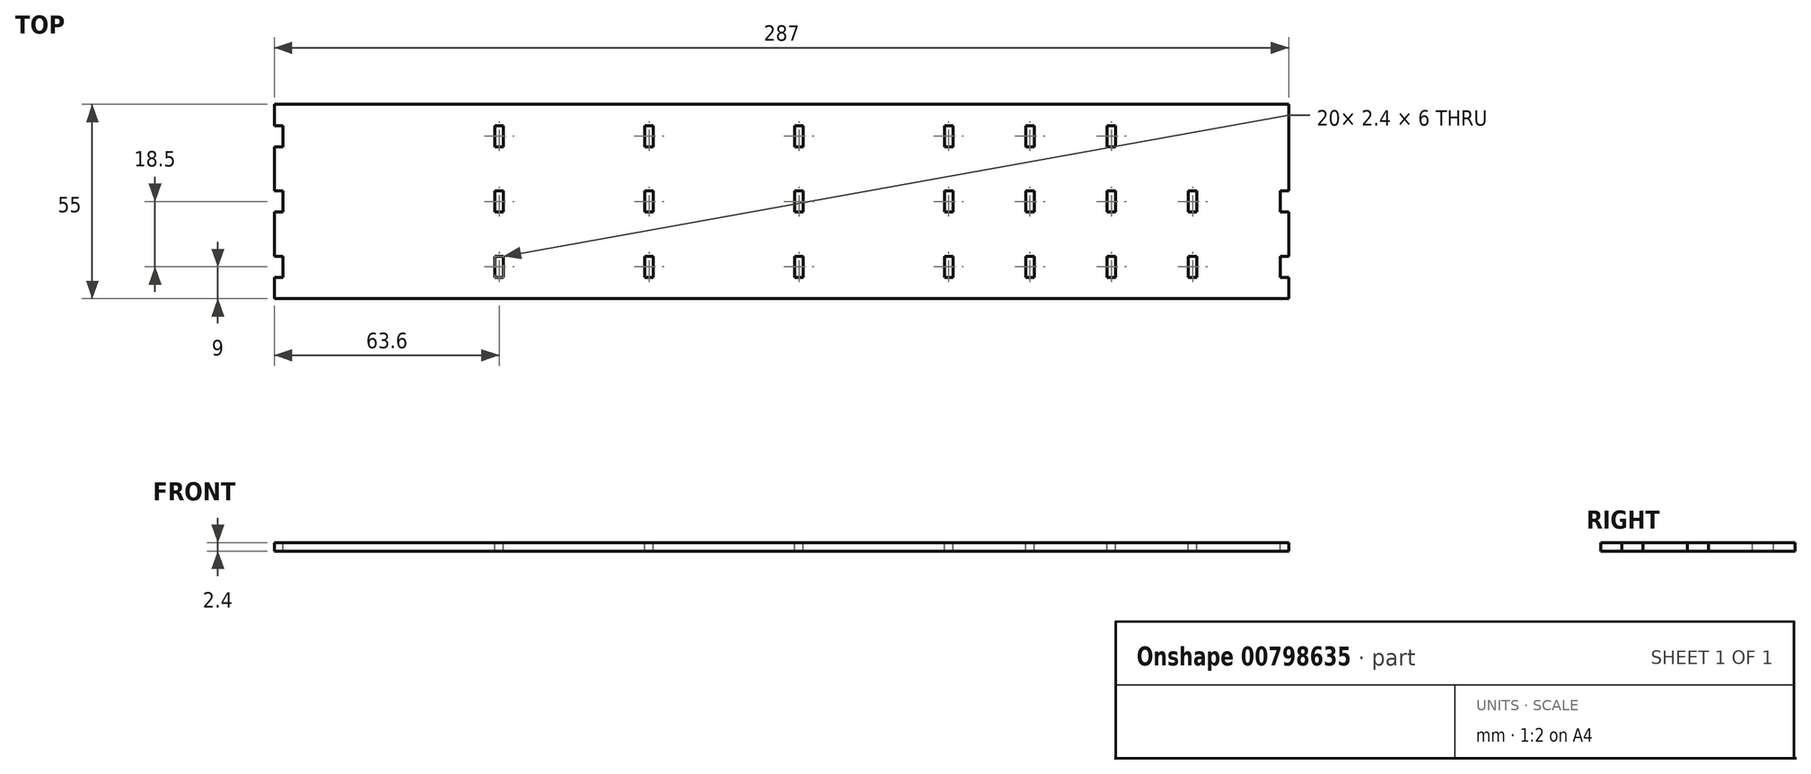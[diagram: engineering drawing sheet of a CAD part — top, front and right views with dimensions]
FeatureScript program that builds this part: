
annotation { "Feature Type Name" : "Feature", "Feature Type Description" : "" }
export const myFeature = defineFeature(function(context is Context, id is Id, definition is map)
    precondition{}
    {
        {
            var Q0;
            Q0=qCreatedBy(makeId("Top.planeOp"),FACE);
            var sketch = newSketch(context, id + "F0", { "sketchPlane" : qUnion([Q0])});
            skLineSegment(sketch, "E0.bottom", {"start": v(143.5, 27.5) * mm, "end": v(-143.5, 27.5) * mm});
            skLineSegment(sketch, "E0.top", {"start": v(143.5, -27.5) * mm, "end": v(-143.5, -27.5) * mm});
            skLineSegment(sketch, "E0.left", {"start": v(143.5, 27.5) * mm, "end": v(143.5, -27.5) * mm});
            skLineSegment(sketch, "E0.right", {"start": v(-143.5, 27.5) * mm, "end": v(-143.5, -27.5) * mm});
            skPoint(sketch, "E0.middle", {"position": v(0, 0) * mm});
            skSolve(sketch);
        }
        {
            var Q0;
            Q0=makeQuery(id+"F0.imprint","IMPRINT",FACE,{"disambiguationData":[TD([[makeQuery(id+"F0.imprint","IMPRINT",EDGE,{"derivedFrom":sQuery(id+"F0.wireOp",EDGE,"E0.bottom")}),1.0]])]});
            extrude(context, id + "F1", {"entities" : qUnion([Q0]), "depth" : 2.4 * mm, "offsetDistance" : 25 * mm});
        }
        {
            var Q0;
            Q0=makeQuery(id+"F1.opExtrude","CAP_FACE",FACE,{"disambiguationData":[OSD([sQuery(id+"F0.wireOp",EDGE,"E0.bottom"),sQuery(id+"F0.wireOp",EDGE,"E0.top"),sQuery(id+"F0.wireOp",EDGE,"E0.left"),sQuery(id+"F0.wireOp",EDGE,"E0.right")])],"isStart":false});
            var sketch = newSketch(context, id + "F2", { "sketchPlane" : qUnion([Q0])});
            skLineSegment(sketch, "E1", {"start": v(-143.5, 0) * mm, "end": v(143.5, 0) * mm, "construction": true});
            skPoint(sketch, "E2", {"position": v(-79.9, 0) * mm});
            skPoint(sketch, "E3", {"position": v(-37.5, 0) * mm});
            skPoint(sketch, "E4", {"position": v(4.9, 0) * mm});
            skPoint(sketch, "E5", {"position": v(47.3, 0) * mm});
            skPoint(sketch, "E6", {"position": v(70.3, 0) * mm});
            skPoint(sketch, "E7", {"position": v(93.3, 0) * mm});
            skPoint(sketch, "E8", {"position": v(116.3, 0) * mm});
            skPoint(sketch, "E9", {"position": v(142.3, 0) * mm});
            skLineSegment(sketch, "E10.bottom", {"start": v(-143.5, -3) * mm, "end": v(-141.1, -3) * mm});
            skLineSegment(sketch, "E10.top", {"start": v(-143.5, 3) * mm, "end": v(-141.1, 3) * mm});
            skLineSegment(sketch, "E10.left", {"start": v(-143.5, -3) * mm, "end": v(-143.5, 3) * mm});
            skLineSegment(sketch, "E10.right", {"start": v(-141.1, -3) * mm, "end": v(-141.1, 3) * mm});
            skPoint(sketch, "E10.middle", {"position": v(-142.3, 0) * mm});
            skLineSegment(sketch, "E11.bottom", {"start": v(-81.1, -3) * mm, "end": v(-78.7, -3) * mm});
            skLineSegment(sketch, "E11.top", {"start": v(-81.1, 3) * mm, "end": v(-78.7, 3) * mm});
            skLineSegment(sketch, "E11.left", {"start": v(-81.1, -3) * mm, "end": v(-81.1, 3) * mm});
            skLineSegment(sketch, "E11.right", {"start": v(-78.7, -3) * mm, "end": v(-78.7, 3) * mm});
            skLineSegment(sketch, "E12.bottom", {"start": v(-38.7, -3) * mm, "end": v(-36.3, -3) * mm});
            skLineSegment(sketch, "E12.top", {"start": v(-38.7, 3) * mm, "end": v(-36.3, 3) * mm});
            skLineSegment(sketch, "E12.left", {"start": v(-38.7, -3) * mm, "end": v(-38.7, 3) * mm});
            skLineSegment(sketch, "E12.right", {"start": v(-36.3, -3) * mm, "end": v(-36.3, 3) * mm});
            skLineSegment(sketch, "E13.bottom", {"start": v(3.7, -3) * mm, "end": v(6.1, -3) * mm});
            skLineSegment(sketch, "E13.top", {"start": v(3.7, 3) * mm, "end": v(6.1, 3) * mm});
            skLineSegment(sketch, "E13.left", {"start": v(3.7, -3) * mm, "end": v(3.7, 3) * mm});
            skLineSegment(sketch, "E13.right", {"start": v(6.1, -3) * mm, "end": v(6.1, 3) * mm});
            skLineSegment(sketch, "E14.bottom", {"start": v(46.1, -3) * mm, "end": v(48.5, -3) * mm});
            skLineSegment(sketch, "E14.top", {"start": v(46.1, 3) * mm, "end": v(48.5, 3) * mm});
            skLineSegment(sketch, "E14.left", {"start": v(46.1, -3) * mm, "end": v(46.1, 3) * mm});
            skLineSegment(sketch, "E14.right", {"start": v(48.5, -3) * mm, "end": v(48.5, 3) * mm});
            skLineSegment(sketch, "E15.bottom", {"start": v(69.1, -3) * mm, "end": v(71.5, -3) * mm});
            skLineSegment(sketch, "E15.top", {"start": v(69.1, 3) * mm, "end": v(71.5, 3) * mm});
            skLineSegment(sketch, "E15.left", {"start": v(69.1, -3) * mm, "end": v(69.1, 3) * mm});
            skLineSegment(sketch, "E15.right", {"start": v(71.5, -3) * mm, "end": v(71.5, 3) * mm});
            skLineSegment(sketch, "E16.bottom", {"start": v(92.1, -3) * mm, "end": v(94.5, -3) * mm});
            skLineSegment(sketch, "E16.top", {"start": v(92.1, 3) * mm, "end": v(94.5, 3) * mm});
            skLineSegment(sketch, "E16.left", {"start": v(92.1, -3) * mm, "end": v(92.1, 3) * mm});
            skLineSegment(sketch, "E16.right", {"start": v(94.5, -3) * mm, "end": v(94.5, 3) * mm});
            skLineSegment(sketch, "E17.bottom", {"start": v(115.1, -3) * mm, "end": v(117.5, -3) * mm});
            skLineSegment(sketch, "E17.top", {"start": v(115.1, 3) * mm, "end": v(117.5, 3) * mm});
            skLineSegment(sketch, "E17.left", {"start": v(115.1, -3) * mm, "end": v(115.1, 3) * mm});
            skLineSegment(sketch, "E17.right", {"start": v(117.5, -3) * mm, "end": v(117.5, 3) * mm});
            skLineSegment(sketch, "E18.bottom", {"start": v(141.1, -3) * mm, "end": v(143.5, -3) * mm});
            skLineSegment(sketch, "E18.top", {"start": v(141.1, 3) * mm, "end": v(143.5, 3) * mm});
            skLineSegment(sketch, "E18.left", {"start": v(141.1, -3) * mm, "end": v(141.1, 3) * mm});
            skLineSegment(sketch, "E18.right", {"start": v(143.5, -3) * mm, "end": v(143.5, 3) * mm});
            skLineSegment(sketch, "E19", {"start": v(-143.5, -18.5) * mm, "end": v(143.5, -18.5) * mm, "construction": true});
            skPoint(sketch, "E20", {"position": v(-79.9, -18.5) * mm});
            skPoint(sketch, "E21", {"position": v(-37.5, -18.5) * mm});
            skPoint(sketch, "E22", {"position": v(4.9, -18.5) * mm});
            skPoint(sketch, "E23", {"position": v(47.3, -18.5) * mm});
            skPoint(sketch, "E24", {"position": v(70.3, -18.5) * mm});
            skPoint(sketch, "E25", {"position": v(93.3, -18.5) * mm});
            skPoint(sketch, "E26", {"position": v(116.3, -18.5) * mm});
            skPoint(sketch, "E27", {"position": v(142.3, -18.5) * mm});
            skLineSegment(sketch, "E28.bottom", {"start": v(-143.5, -21.5) * mm, "end": v(-141.1, -21.5) * mm});
            skLineSegment(sketch, "E28.top", {"start": v(-143.5, -15.5) * mm, "end": v(-141.1, -15.5) * mm});
            skLineSegment(sketch, "E28.left", {"start": v(-143.5, -21.5) * mm, "end": v(-143.5, -15.5) * mm});
            skLineSegment(sketch, "E28.right", {"start": v(-141.1, -21.5) * mm, "end": v(-141.1, -15.5) * mm});
            skPoint(sketch, "E28.middle", {"position": v(-142.3, -18.5) * mm});
            skLineSegment(sketch, "E29.bottom", {"start": v(-81.1, -21.5) * mm, "end": v(-78.7, -21.5) * mm});
            skLineSegment(sketch, "E29.top", {"start": v(-81.1, -15.5) * mm, "end": v(-78.7, -15.5) * mm});
            skLineSegment(sketch, "E29.left", {"start": v(-81.1, -21.5) * mm, "end": v(-81.1, -15.5) * mm});
            skLineSegment(sketch, "E29.right", {"start": v(-78.7, -21.5) * mm, "end": v(-78.7, -15.5) * mm});
            skLineSegment(sketch, "E30.bottom", {"start": v(-38.7, -21.5) * mm, "end": v(-36.3, -21.5) * mm});
            skLineSegment(sketch, "E30.top", {"start": v(-38.7, -15.5) * mm, "end": v(-36.3, -15.5) * mm});
            skLineSegment(sketch, "E30.left", {"start": v(-38.7, -21.5) * mm, "end": v(-38.7, -15.5) * mm});
            skLineSegment(sketch, "E30.right", {"start": v(-36.3, -21.5) * mm, "end": v(-36.3, -15.5) * mm});
            skLineSegment(sketch, "E31.bottom", {"start": v(3.7, -21.5) * mm, "end": v(6.1, -21.5) * mm});
            skLineSegment(sketch, "E31.top", {"start": v(3.7, -15.5) * mm, "end": v(6.1, -15.5) * mm});
            skLineSegment(sketch, "E31.left", {"start": v(3.7, -21.5) * mm, "end": v(3.7, -15.5) * mm});
            skLineSegment(sketch, "E31.right", {"start": v(6.1, -21.5) * mm, "end": v(6.1, -15.5) * mm});
            skLineSegment(sketch, "E32.bottom", {"start": v(46.1, -21.5) * mm, "end": v(48.5, -21.5) * mm});
            skLineSegment(sketch, "E32.top", {"start": v(46.1, -15.5) * mm, "end": v(48.5, -15.5) * mm});
            skLineSegment(sketch, "E32.left", {"start": v(46.1, -21.5) * mm, "end": v(46.1, -15.5) * mm});
            skLineSegment(sketch, "E32.right", {"start": v(48.5, -21.5) * mm, "end": v(48.5, -15.5) * mm});
            skLineSegment(sketch, "E33.bottom", {"start": v(69.1, -21.5) * mm, "end": v(71.5, -21.5) * mm});
            skLineSegment(sketch, "E33.top", {"start": v(69.1, -15.5) * mm, "end": v(71.5, -15.5) * mm});
            skLineSegment(sketch, "E33.left", {"start": v(69.1, -21.5) * mm, "end": v(69.1, -15.5) * mm});
            skLineSegment(sketch, "E33.right", {"start": v(71.5, -21.5) * mm, "end": v(71.5, -15.5) * mm});
            skLineSegment(sketch, "E34.bottom", {"start": v(92.1, -21.5) * mm, "end": v(94.5, -21.5) * mm});
            skLineSegment(sketch, "E34.top", {"start": v(92.1, -15.5) * mm, "end": v(94.5, -15.5) * mm});
            skLineSegment(sketch, "E34.left", {"start": v(92.1, -21.5) * mm, "end": v(92.1, -15.5) * mm});
            skLineSegment(sketch, "E34.right", {"start": v(94.5, -21.5) * mm, "end": v(94.5, -15.5) * mm});
            skLineSegment(sketch, "E35.bottom", {"start": v(115.1, -21.5) * mm, "end": v(117.5, -21.5) * mm});
            skLineSegment(sketch, "E35.top", {"start": v(115.1, -15.5) * mm, "end": v(117.5, -15.5) * mm});
            skLineSegment(sketch, "E35.left", {"start": v(115.1, -21.5) * mm, "end": v(115.1, -15.5) * mm});
            skLineSegment(sketch, "E35.right", {"start": v(117.5, -21.5) * mm, "end": v(117.5, -15.5) * mm});
            skLineSegment(sketch, "E36.bottom", {"start": v(141.1, -21.5) * mm, "end": v(143.5, -21.5) * mm});
            skLineSegment(sketch, "E36.top", {"start": v(141.1, -15.5) * mm, "end": v(143.5, -15.5) * mm});
            skLineSegment(sketch, "E36.left", {"start": v(141.1, -21.5) * mm, "end": v(141.1, -15.5) * mm});
            skLineSegment(sketch, "E36.right", {"start": v(143.5, -21.5) * mm, "end": v(143.5, -15.5) * mm});
            skLineSegment(sketch, "E37.MirrorCS", {"start": v(-143.5, -15.5) * mm, "end": v(-143.5, -21.5) * mm});
            skLineSegment(sketch, "E38.MirrorCS", {"start": v(71.5, -15.5) * mm, "end": v(71.5, -21.5) * mm});
            skLineSegment(sketch, "E39.MirrorCS", {"start": v(115.1, -15.5) * mm, "end": v(115.1, -21.5) * mm});
            skLineSegment(sketch, "E40.MirrorCS", {"start": v(-141.1, -15.5) * mm, "end": v(-141.1, -21.5) * mm});
            skLineSegment(sketch, "E41.MirrorCS", {"start": v(48.5, -15.5) * mm, "end": v(48.5, -21.5) * mm});
            skLineSegment(sketch, "E42.MirrorCS", {"start": v(143.5, -15.5) * mm, "end": v(143.5, -21.5) * mm});
            skLineSegment(sketch, "E43.MirrorCS", {"start": v(-36.3, -15.5) * mm, "end": v(-36.3, -21.5) * mm});
            skLineSegment(sketch, "E44.MirrorCS", {"start": v(94.5, -15.5) * mm, "end": v(94.5, -21.5) * mm});
            skLineSegment(sketch, "E45.MirrorCS", {"start": v(-78.7, -15.5) * mm, "end": v(-78.7, -21.5) * mm});
            skLineSegment(sketch, "E46.MirrorCS", {"start": v(3.7, -15.5) * mm, "end": v(3.7, -21.5) * mm});
            skLineSegment(sketch, "E47.MirrorCS", {"start": v(69.1, -15.5) * mm, "end": v(69.1, -21.5) * mm});
            skLineSegment(sketch, "E48.MirrorCS", {"start": v(-81.1, -15.5) * mm, "end": v(-81.1, -21.5) * mm});
            skLineSegment(sketch, "E49.MirrorCS", {"start": v(46.1, -15.5) * mm, "end": v(46.1, -21.5) * mm});
            skLineSegment(sketch, "E50.MirrorCS", {"start": v(117.5, -15.5) * mm, "end": v(117.5, -21.5) * mm});
            skLineSegment(sketch, "E51.MirrorCS", {"start": v(6.1, -15.5) * mm, "end": v(6.1, -21.5) * mm});
            skLineSegment(sketch, "E52.MirrorCS", {"start": v(141.1, -15.5) * mm, "end": v(141.1, -21.5) * mm});
            skLineSegment(sketch, "E53.MirrorCS", {"start": v(92.1, -15.5) * mm, "end": v(92.1, -21.5) * mm});
            skLineSegment(sketch, "E54.MirrorCS", {"start": v(-38.7, -15.5) * mm, "end": v(-38.7, -21.5) * mm});
            skLineSegment(sketch, "E55.MirrorCS", {"start": v(141.1, 21.5) * mm, "end": v(143.5, 21.5) * mm});
            skLineSegment(sketch, "E56.MirrorCS", {"start": v(143.5, 15.5) * mm, "end": v(143.5, 21.5) * mm});
            skLineSegment(sketch, "E57.MirrorCS", {"start": v(-143.5, 15.5) * mm, "end": v(-141.1, 15.5) * mm});
            skLineSegment(sketch, "E58.MirrorCS", {"start": v(141.1, 21.5) * mm, "end": v(141.1, 15.5) * mm});
            skLineSegment(sketch, "E59.MirrorCS", {"start": v(-141.1, 21.5) * mm, "end": v(-141.1, 15.5) * mm});
            skLineSegment(sketch, "E60.MirrorCS", {"start": v(-81.1, 15.5) * mm, "end": v(-78.7, 15.5) * mm});
            skLineSegment(sketch, "E61.MirrorCS", {"start": v(-143.5, 15.5) * mm, "end": v(-143.5, 21.5) * mm});
            skLineSegment(sketch, "E62.MirrorCS", {"start": v(-143.5, 21.5) * mm, "end": v(-141.1, 21.5) * mm});
            skLineSegment(sketch, "E63.MirrorCS", {"start": v(46.1, 15.5) * mm, "end": v(46.1, 21.5) * mm});
            skLineSegment(sketch, "E64.MirrorCS", {"start": v(92.1, 15.5) * mm, "end": v(94.5, 15.5) * mm});
            skLineSegment(sketch, "E65.MirrorCS", {"start": v(141.1, 15.5) * mm, "end": v(143.5, 15.5) * mm});
            skLineSegment(sketch, "E66.MirrorCS", {"start": v(-38.7, 21.5) * mm, "end": v(-36.3, 21.5) * mm});
            skLineSegment(sketch, "E67.MirrorCS", {"start": v(46.1, 21.5) * mm, "end": v(48.5, 21.5) * mm});
            skLineSegment(sketch, "E68.MirrorCS", {"start": v(115.1, 21.5) * mm, "end": v(117.5, 21.5) * mm});
            skLineSegment(sketch, "E69.MirrorCS", {"start": v(94.5, 21.5) * mm, "end": v(94.5, 15.5) * mm});
            skLineSegment(sketch, "E70.MirrorCS", {"start": v(117.5, 21.5) * mm, "end": v(117.5, 15.5) * mm});
            skLineSegment(sketch, "E71.MirrorCS", {"start": v(3.7, 15.5) * mm, "end": v(3.7, 21.5) * mm});
            skLineSegment(sketch, "E72.MirrorCS", {"start": v(69.1, 21.5) * mm, "end": v(71.5, 21.5) * mm});
            skLineSegment(sketch, "E73.MirrorCS", {"start": v(92.1, 15.5) * mm, "end": v(92.1, 21.5) * mm});
            skLineSegment(sketch, "E74.MirrorCS", {"start": v(-81.1, 21.5) * mm, "end": v(-81.1, 15.5) * mm});
            skLineSegment(sketch, "E75.MirrorCS", {"start": v(-36.3, 21.5) * mm, "end": v(-36.3, 15.5) * mm});
            skLineSegment(sketch, "E76.MirrorCS", {"start": v(69.1, 21.5) * mm, "end": v(69.1, 15.5) * mm});
            skLineSegment(sketch, "E77.MirrorCS", {"start": v(48.5, 15.5) * mm, "end": v(48.5, 21.5) * mm});
            skLineSegment(sketch, "E78.MirrorCS", {"start": v(143.5, 21.5) * mm, "end": v(143.5, 15.5) * mm});
            skLineSegment(sketch, "E79.MirrorCS", {"start": v(-38.7, 15.5) * mm, "end": v(-36.3, 15.5) * mm});
            skLineSegment(sketch, "E80.MirrorCS", {"start": v(-38.7, 21.5) * mm, "end": v(-38.7, 15.5) * mm});
            skLineSegment(sketch, "E81.MirrorCS", {"start": v(-81.1, 21.5) * mm, "end": v(-78.7, 21.5) * mm});
            skLineSegment(sketch, "E82.MirrorCS", {"start": v(92.1, 21.5) * mm, "end": v(94.5, 21.5) * mm});
            skLineSegment(sketch, "E83.MirrorCS", {"start": v(141.1, 15.5) * mm, "end": v(141.1, 21.5) * mm});
            skLineSegment(sketch, "E84.MirrorCS", {"start": v(115.1, 21.5) * mm, "end": v(115.1, 15.5) * mm});
            skLineSegment(sketch, "E85.MirrorCS", {"start": v(46.1, 15.5) * mm, "end": v(48.5, 15.5) * mm});
            skLineSegment(sketch, "E86.MirrorCS", {"start": v(69.1, 15.5) * mm, "end": v(71.5, 15.5) * mm});
            skLineSegment(sketch, "E87.MirrorCS", {"start": v(3.7, 15.5) * mm, "end": v(6.1, 15.5) * mm});
            skLineSegment(sketch, "E88.MirrorCS", {"start": v(71.5, 21.5) * mm, "end": v(71.5, 15.5) * mm});
            skLineSegment(sketch, "E89.MirrorCS", {"start": v(6.1, 21.5) * mm, "end": v(6.1, 15.5) * mm});
            skLineSegment(sketch, "E90.MirrorCS", {"start": v(-78.7, 15.5) * mm, "end": v(-78.7, 21.5) * mm});
            skLineSegment(sketch, "E91.MirrorCS", {"start": v(-141.1, 15.5) * mm, "end": v(-141.1, 21.5) * mm});
            skLineSegment(sketch, "E92.MirrorCS", {"start": v(115.1, 15.5) * mm, "end": v(117.5, 15.5) * mm});
            skLineSegment(sketch, "E93.MirrorCS", {"start": v(3.7, 21.5) * mm, "end": v(6.1, 21.5) * mm});
            skLineSegment(sketch, "E94.MirrorCS", {"start": v(-143.5, 21.5) * mm, "end": v(-143.5, 15.5) * mm});
            skLineSegment(sketch, "E95.MirrorCS", {"start": v(92.1, 21.5) * mm, "end": v(92.1, 15.5) * mm});
            skLineSegment(sketch, "E96.MirrorCS", {"start": v(-78.7, 21.5) * mm, "end": v(-78.7, 15.5) * mm});
            skLineSegment(sketch, "E97.MirrorCS", {"start": v(94.5, 15.5) * mm, "end": v(94.5, 21.5) * mm});
            skLineSegment(sketch, "E98.MirrorCS", {"start": v(71.5, 15.5) * mm, "end": v(71.5, 21.5) * mm});
            skLineSegment(sketch, "E99.MirrorCS", {"start": v(6.1, 15.5) * mm, "end": v(6.1, 21.5) * mm});
            skLineSegment(sketch, "E100.MirrorCS", {"start": v(3.7, 21.5) * mm, "end": v(3.7, 15.5) * mm});
            skLineSegment(sketch, "E101.MirrorCS", {"start": v(-38.7, 15.5) * mm, "end": v(-38.7, 21.5) * mm});
            skLineSegment(sketch, "E102.MirrorCS", {"start": v(-36.3, 15.5) * mm, "end": v(-36.3, 21.5) * mm});
            skLineSegment(sketch, "E103.MirrorCS", {"start": v(-81.1, 15.5) * mm, "end": v(-81.1, 21.5) * mm});
            skLineSegment(sketch, "E104.MirrorCS", {"start": v(115.1, 15.5) * mm, "end": v(115.1, 21.5) * mm});
            skLineSegment(sketch, "E105.MirrorCS", {"start": v(69.1, 15.5) * mm, "end": v(69.1, 21.5) * mm});
            skLineSegment(sketch, "E106.MirrorCS", {"start": v(48.5, 21.5) * mm, "end": v(48.5, 15.5) * mm});
            skLineSegment(sketch, "E107.MirrorCS", {"start": v(117.5, 15.5) * mm, "end": v(117.5, 21.5) * mm});
            skLineSegment(sketch, "E108.MirrorCS", {"start": v(46.1, 21.5) * mm, "end": v(46.1, 15.5) * mm});
            skPoint(sketch, "E109.MirrorP", {"position": v(4.9, 18.5) * mm});
            skPoint(sketch, "E110.MirrorP", {"position": v(116.3, 18.5) * mm});
            skPoint(sketch, "E111.MirrorP", {"position": v(70.3, 18.5) * mm});
            skPoint(sketch, "E112.MirrorP", {"position": v(47.3, 18.5) * mm});
            skPoint(sketch, "E113.MirrorP", {"position": v(142.3, 18.5) * mm});
            skPoint(sketch, "E114.MirrorP", {"position": v(-79.9, 18.5) * mm});
            skPoint(sketch, "E115.MirrorP", {"position": v(-37.5, 18.5) * mm});
            skPoint(sketch, "E116.MirrorP", {"position": v(93.3, 18.5) * mm});
            skPoint(sketch, "E117.MirrorP", {"position": v(-142.3, 18.5) * mm});
            skLineSegment(sketch, "E118.MirrorCS", {"start": v(-143.5, 18.5) * mm, "end": v(143.5, 18.5) * mm, "construction": true});
            skSolve(sketch);
        }
        {
            var Q0;
            Q0=makeQuery(id+"F2.imprint","IMPRINT",FACE,{"disambiguationData":[TD([[makeQuery(id+"F2.imprint","IMPRINT",EDGE,{"derivedFrom":sQuery(id+"F2.wireOp",EDGE,"E10.bottom")}),1.0]])]});
            var Q1;
            Q1=makeQuery(id+"F2.imprint","IMPRINT",FACE,{"disambiguationData":[TD([[makeQuery(id+"F2.imprint","IMPRINT",EDGE,{"derivedFrom":sQuery(id+"F2.wireOp",EDGE,"E28.bottom")}),1.0]])]});
            var Q2;
            Q2=makeQuery(id+"F2.imprint","IMPRINT",FACE,{"disambiguationData":[TD([[makeQuery(id+"F2.imprint","IMPRINT",EDGE,{"derivedFrom":sQuery(id+"F2.wireOp",EDGE,"E62.MirrorCS")}),-1.0]])]});
            var Q3;
            Q3=makeQuery(id+"F2.imprint","IMPRINT",FACE,{"disambiguationData":[TD([[makeQuery(id+"F2.imprint","IMPRINT",EDGE,{"derivedFrom":sQuery(id+"F2.wireOp",EDGE,"E60.MirrorCS")}),1.0]])]});
            var Q4;
            Q4=makeQuery(id+"F2.imprint","IMPRINT",FACE,{"disambiguationData":[TD([[makeQuery(id+"F2.imprint","IMPRINT",EDGE,{"derivedFrom":sQuery(id+"F2.wireOp",EDGE,"E11.bottom")}),1.0]])]});
            var Q5;
            Q5=makeQuery(id+"F2.imprint","IMPRINT",FACE,{"disambiguationData":[TD([[makeQuery(id+"F2.imprint","IMPRINT",EDGE,{"derivedFrom":sQuery(id+"F2.wireOp",EDGE,"E29.bottom")}),1.0]])]});
            var Q6;
            Q6=makeQuery(id+"F2.imprint","IMPRINT",FACE,{"disambiguationData":[TD([[makeQuery(id+"F2.imprint","IMPRINT",EDGE,{"derivedFrom":sQuery(id+"F2.wireOp",EDGE,"E30.right")}),1.0]])]});
            var Q7;
            Q7=makeQuery(id+"F2.imprint","IMPRINT",FACE,{"disambiguationData":[TD([[makeQuery(id+"F2.imprint","IMPRINT",EDGE,{"derivedFrom":sQuery(id+"F2.wireOp",EDGE,"E12.bottom")}),1.0]])]});
            var Q8;
            Q8=makeQuery(id+"F2.imprint","IMPRINT",FACE,{"disambiguationData":[TD([[makeQuery(id+"F2.imprint","IMPRINT",EDGE,{"derivedFrom":sQuery(id+"F2.wireOp",EDGE,"E79.MirrorCS")}),1.0]])]});
            var Q9;
            Q9=makeQuery(id+"F2.imprint","IMPRINT",FACE,{"disambiguationData":[TD([[makeQuery(id+"F2.imprint","IMPRINT",EDGE,{"derivedFrom":sQuery(id+"F2.wireOp",EDGE,"E87.MirrorCS")}),1.0]])]});
            var Q10;
            Q10=makeQuery(id+"F2.imprint","IMPRINT",FACE,{"disambiguationData":[TD([[makeQuery(id+"F2.imprint","IMPRINT",EDGE,{"derivedFrom":sQuery(id+"F2.wireOp",EDGE,"E13.bottom")}),1.0]])]});
            var Q11;
            Q11=makeQuery(id+"F2.imprint","IMPRINT",FACE,{"disambiguationData":[TD([[makeQuery(id+"F2.imprint","IMPRINT",EDGE,{"derivedFrom":sQuery(id+"F2.wireOp",EDGE,"E31.right")}),1.0]])]});
            var Q12;
            Q12=makeQuery(id+"F2.imprint","IMPRINT",FACE,{"disambiguationData":[TD([[makeQuery(id+"F2.imprint","IMPRINT",EDGE,{"derivedFrom":sQuery(id+"F2.wireOp",EDGE,"E32.bottom")}),1.0]])]});
            var Q13;
            Q13=makeQuery(id+"F2.imprint","IMPRINT",FACE,{"disambiguationData":[TD([[makeQuery(id+"F2.imprint","IMPRINT",EDGE,{"derivedFrom":sQuery(id+"F2.wireOp",EDGE,"E14.bottom")}),1.0]])]});
            var Q14;
            Q14=makeQuery(id+"F2.imprint","IMPRINT",FACE,{"disambiguationData":[TD([[makeQuery(id+"F2.imprint","IMPRINT",EDGE,{"derivedFrom":sQuery(id+"F2.wireOp",EDGE,"E67.MirrorCS")}),-1.0]])]});
            var Q15;
            Q15=makeQuery(id+"F2.imprint","IMPRINT",FACE,{"disambiguationData":[TD([[makeQuery(id+"F2.imprint","IMPRINT",EDGE,{"derivedFrom":sQuery(id+"F2.wireOp",EDGE,"E72.MirrorCS")}),-1.0]])]});
            var Q16;
            Q16=makeQuery(id+"F2.imprint","IMPRINT",FACE,{"disambiguationData":[TD([[makeQuery(id+"F2.imprint","IMPRINT",EDGE,{"derivedFrom":sQuery(id+"F2.wireOp",EDGE,"E15.bottom")}),1.0]])]});
            var Q17;
            Q17=makeQuery(id+"F2.imprint","IMPRINT",FACE,{"disambiguationData":[TD([[makeQuery(id+"F2.imprint","IMPRINT",EDGE,{"derivedFrom":sQuery(id+"F2.wireOp",EDGE,"E33.bottom")}),1.0]])]});
            var Q18;
            Q18=makeQuery(id+"F2.imprint","IMPRINT",FACE,{"disambiguationData":[TD([[makeQuery(id+"F2.imprint","IMPRINT",EDGE,{"derivedFrom":sQuery(id+"F2.wireOp",EDGE,"E34.bottom")}),1.0]])]});
            var Q19;
            Q19=makeQuery(id+"F2.imprint","IMPRINT",FACE,{"disambiguationData":[TD([[makeQuery(id+"F2.imprint","IMPRINT",EDGE,{"derivedFrom":sQuery(id+"F2.wireOp",EDGE,"E16.bottom")}),1.0]])]});
            var Q20;
            Q20=makeQuery(id+"F2.imprint","IMPRINT",FACE,{"disambiguationData":[TD([[makeQuery(id+"F2.imprint","IMPRINT",EDGE,{"derivedFrom":sQuery(id+"F2.wireOp",EDGE,"E82.MirrorCS")}),-1.0]])]});
            var Q21;
            Q21=makeQuery(id+"F2.imprint","IMPRINT",FACE,{"disambiguationData":[TD([[makeQuery(id+"F2.imprint","IMPRINT",EDGE,{"derivedFrom":sQuery(id+"F2.wireOp",EDGE,"E107.MirrorCS")}),1.0]])]});
            var Q22;
            Q22=makeQuery(id+"F2.imprint","IMPRINT",FACE,{"disambiguationData":[TD([[makeQuery(id+"F2.imprint","IMPRINT",EDGE,{"derivedFrom":sQuery(id+"F2.wireOp",EDGE,"E17.bottom")}),1.0]])]});
            var Q23;
            Q23=makeQuery(id+"F2.imprint","IMPRINT",FACE,{"disambiguationData":[TD([[makeQuery(id+"F2.imprint","IMPRINT",EDGE,{"derivedFrom":sQuery(id+"F2.wireOp",EDGE,"E35.top")}),-1.0]])]});
            var Q24;
            Q24=makeQuery(id+"F2.imprint","IMPRINT",FACE,{"disambiguationData":[TD([[makeQuery(id+"F2.imprint","IMPRINT",EDGE,{"derivedFrom":sQuery(id+"F2.wireOp",EDGE,"E83.MirrorCS")}),-1.0]])]});
            var Q25;
            Q25=makeQuery(id+"F2.imprint","IMPRINT",FACE,{"disambiguationData":[TD([[makeQuery(id+"F2.imprint","IMPRINT",EDGE,{"derivedFrom":sQuery(id+"F2.wireOp",EDGE,"E18.bottom")}),1.0]])]});
            var Q26;
            Q26=makeQuery(id+"F2.imprint","IMPRINT",FACE,{"disambiguationData":[TD([[makeQuery(id+"F2.imprint","IMPRINT",EDGE,{"derivedFrom":sQuery(id+"F2.wireOp",EDGE,"E36.top")}),-1.0]])]});
            extrude(context, id + "F3", {"entities" : qUnion([Q0, Q1, Q2, Q3, Q4, Q5, Q6, Q7, Q8, Q9, Q10, Q11, Q12, Q13, Q14, Q15, Q16, Q17, Q18, Q19, Q20, Q21, Q22, Q23, Q24, Q25, Q26]), "operationType" : NewBodyOperationType.REMOVE, "endBound" : BoundingType.THROUGH_ALL, "oppositeDirection" : true, "depth" : 25 * mm, "offsetDistance" : 25 * mm});
        }
    });
